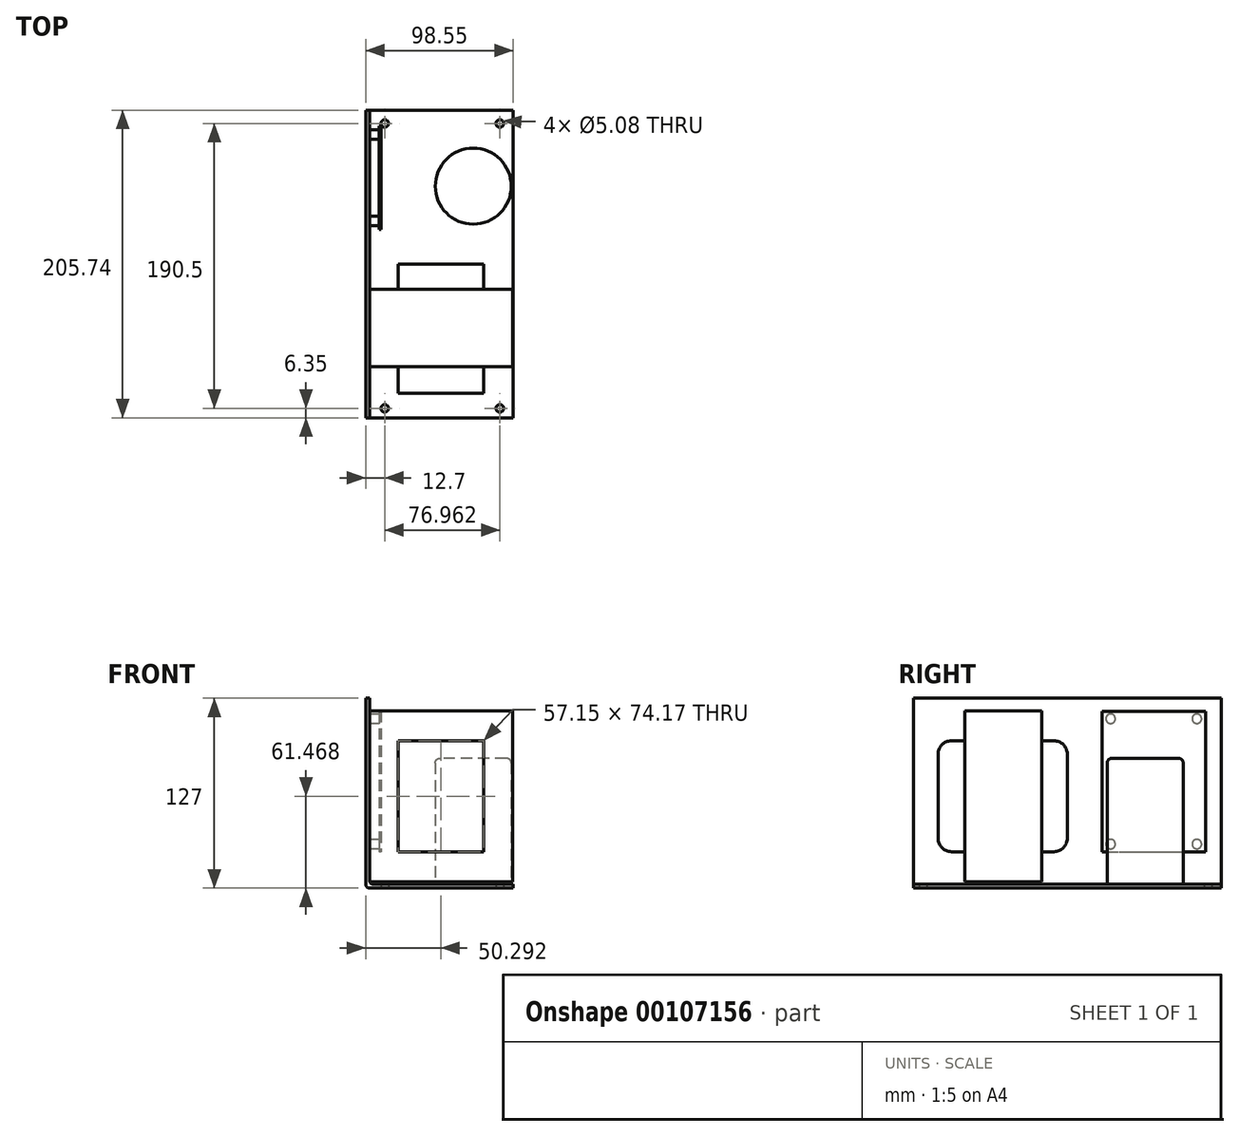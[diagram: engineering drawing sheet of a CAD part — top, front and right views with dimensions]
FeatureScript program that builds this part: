
annotation { "Feature Type Name" : "Feature", "Feature Type Description" : "" }
export const myFeature = defineFeature(function(context is Context, id is Id, definition is map)
    precondition{}
    {
        {
            var Q0;
            Q0=qCreatedBy(makeId("Front.planeOp"),FACE);
            var sketch = newSketch(context, id + "F0", { "sketchPlane" : qUnion([Q0])});
            skLineSegment(sketch, "E0.bottom", {"start": v(0, 0) * mm, "end": v(98.55, 0) * mm});
            skLineSegment(sketch, "E0.left", {"start": v(0, 0) * mm, "end": v(0, 127) * mm});
            skLineSegment(sketch, "E1.0", {"start": v(2.54, 2.54) * mm, "end": v(2.54, 127) * mm});
            skLineSegment(sketch, "E1.1", {"start": v(2.54, 2.54) * mm, "end": v(98.55, 2.54) * mm});
            skLineSegment(sketch, "E2", {"start": v(0, 127) * mm, "end": v(2.54, 127) * mm});
            skLineSegment(sketch, "E3", {"start": v(98.55, 2.54) * mm, "end": v(98.55, 0) * mm});
            skSolve(sketch);
        }
        {
            var Q0;
            Q0 = qSketchRegion(id + "F0", true);
            extrude(context, id + "F1", {"entities" : qUnion([Q0]), "depth" : 205.74 * mm});
        }
        {
            var Q0;
            Q0=makeQuery(id+"F1.opExtrude","SWEPT_FACE",FACE,{"disambiguationData":[OSD([sQuery(id+"F0.wireOp",EDGE,"E0.bottom")])]});
            var sketch = newSketch(context, id + "F2", { "sketchPlane" : qUnion([Q0])});
            skLineSegment(sketch, "E4.bottom", {"start": v(12.7, 199.4) * mm, "end": v(89.66, 199.4) * mm, "construction": true});
            skLineSegment(sketch, "E4.top", {"start": v(12.7, 8.89) * mm, "end": v(89.66, 8.89) * mm, "construction": true});
            skLineSegment(sketch, "E4.left", {"start": v(12.7, 199.4) * mm, "end": v(12.7, 8.89) * mm, "construction": true});
            skLineSegment(sketch, "E4.right", {"start": v(89.66, 199.4) * mm, "end": v(89.66, 8.89) * mm, "construction": true});
            skPoint(sketch, "E4.middle", {"position": v(51.18, 104.14) * mm});
            skSolve(sketch);
        }
        {
            var Q0;
            Q0=sQuery(id+"F2.wireOp",VERTEX,"E4.left.start");
            var Q1;
            Q1=sQuery(id+"F2.wireOp",VERTEX,"E4.right.start");
            var Q2;
            Q2=sQuery(id+"F2.wireOp",VERTEX,"E4.top.end");
            var Q3;
            Q3=sQuery(id+"F2.wireOp",VERTEX,"E4.left.end");
            var Q4;
            Q4=makeQuery(id+"F1.opExtrude","SWEPT_BODY",BODY,{"disambiguationData":[OSD([sQuery(id+"F0.wireOp",EDGE,"E0.bottom"),sQuery(id+"F0.wireOp",EDGE,"E0.left"),sQuery(id+"F0.wireOp",EDGE,"E1.0"),sQuery(id+"F0.wireOp",EDGE,"E1.1"),sQuery(id+"F0.wireOp",EDGE,"E2"),sQuery(id+"F0.wireOp",EDGE,"E3")])]});
            hole(context, id + "F3", {"style" : HoleStyle.SIMPLE, "endStyle" : HoleEndStyle.THROUGH, "holeDiameter" : 5.08 * mm, "locations" : qUnion([Q0, Q1, Q2, Q3]), "scope" : qUnion([Q4]), "isTappedThrough" : true});
        }
        {
            var Q0;
            Q0=makeQuery(id+"F1.opExtrude","SWEPT_EDGE",EDGE,{"disambiguationData":[OSD([sQuery(id+"F0.wireOp",EDGE,"E0.bottom"),sQuery(id+"F0.wireOp",EDGE,"E0.left")])]});
            var Q1;
            Q1=makeQuery(id+"F1.opExtrude","SWEPT_EDGE",EDGE,{"disambiguationData":[OSD([sQuery(id+"F0.wireOp",EDGE,"E1.0"),sQuery(id+"F0.wireOp",EDGE,"E1.1")])]});
            fillet(context, id + "F4", {"entities" : qUnion([Q0, Q1]), "radius" : 2.54 * mm, "tangentPropagation" : true, "allowEdgeOverflow" : false});
        }
        {
            var Q0;
            Q0=makeQuery(id+"F1.opExtrude","SWEPT_FACE",FACE,{"disambiguationData":[OSD([sQuery(id+"F0.wireOp",EDGE,"E1.0")])]});
            var sketch = newSketch(context, id + "F5", { "sketchPlane" : qUnion([Q0])});
            skLineSegment(sketch, "E5.bottom", {"start": v(-171.45, 118.62) * mm, "end": v(-119.89, 118.62) * mm});
            skLineSegment(sketch, "E5.top", {"start": v(-171.45, 4.32) * mm, "end": v(-119.89, 4.32) * mm});
            skLineSegment(sketch, "E5.left", {"start": v(-171.45, 118.62) * mm, "end": v(-171.45, 4.32) * mm});
            skLineSegment(sketch, "E5.right", {"start": v(-119.89, 118.62) * mm, "end": v(-119.89, 4.32) * mm});
            skSolve(sketch);
        }
        {
            var Q0;
            Q0 = qSketchRegion(id + "F5", true);
            extrude(context, id + "F6", {"entities" : qUnion([Q0]), "operationType" : NewBodyOperationType.ADD, "depth" : 95.5 * mm});
        }
        {
            var Q0;
            Q0=makeQuery(id+"F6.opExtrude","SWEPT_FACE",FACE,{"disambiguationData":[OSD([sQuery(id+"F5.wireOp",EDGE,"E5.left")])]});
            var sketch = newSketch(context, id + "F7", { "sketchPlane" : qUnion([Q0])});
            skLineSegment(sketch, "E6.bottom", {"start": v(21.72, 98.55) * mm, "end": v(78.87, 98.55) * mm});
            skLineSegment(sketch, "E6.top", {"start": v(21.72, 24.38) * mm, "end": v(78.87, 24.38) * mm});
            skLineSegment(sketch, "E6.left", {"start": v(21.72, 98.55) * mm, "end": v(21.72, 24.38) * mm});
            skLineSegment(sketch, "E6.right", {"start": v(78.87, 98.55) * mm, "end": v(78.87, 24.38) * mm});
            skPoint(sketch, "E6.middle", {"position": v(50.3, 61.47) * mm});
            skPoint(sketch, "E6.middle.positionSnap0", {"position": v(98.04, 61.47) * mm});
            skPoint(sketch, "E6.middle.positionSnap1", {"position": v(50.3, 118.62) * mm});
            skPoint(sketch, "E6.centerSnap0", {"position": v(98.04, 61.47) * mm});
            skPoint(sketch, "E6.centerSnap1", {"position": v(50.3, 118.62) * mm});
            skSolve(sketch);
        }
        {
            var Q0;
            Q0 = qSketchRegion(id + "F7", true);
            extrude(context, id + "F8", {"entities" : qUnion([Q0]), "operationType" : NewBodyOperationType.ADD, "depth" : 17.78 * mm, "hasSecondDirection" : true, "secondDirectionOppositeDirection" : true, "secondDirectionDepth" : 68.58 * mm});
        }
        {
            var Q0;
            Q0=makeQuery(id+"F1.opExtrude","SWEPT_FACE",FACE,{"disambiguationData":[OSD([sQuery(id+"F0.wireOp",EDGE,"E1.1")])]});
            var sketch = newSketch(context, id + "F9", { "sketchPlane" : qUnion([Q0])});
            skCircle(sketch, "E7", {"center": v(71.88, -50.8) * mm, "radius": 25.4 * mm});
            skSolve(sketch);
        }
        {
            var Q0;
            Q0 = qSketchRegion(id + "F9", true);
            extrude(context, id + "F10", {"entities" : qUnion([Q0]), "operationType" : NewBodyOperationType.ADD, "depth" : 84.33 * mm});
        }
        {
            var Q0;
            Q0=makeQuery(id+"F10.opExtrude","CAP_EDGE",EDGE,{"disambiguationData":[OSD([sQuery(id+"F9.wireOp",EDGE,"E7")])],"isStart":false});
            fillet(context, id + "F11", {"entities" : qUnion([Q0]), "radius" : 3.17 * mm, "tangentPropagation" : true, "allowEdgeOverflow" : false});
        }
        {
            var Q0;
            Q0=makeQuery(id+"F8.opExtrude","CAP_EDGE",EDGE,{"disambiguationData":[OSD([sQuery(id+"F7.wireOp",EDGE,"E6.bottom")])],"isStart":false});
            var Q1;
            Q1=makeQuery(id+"F8.opExtrude","CAP_EDGE",EDGE,{"disambiguationData":[OSD([sQuery(id+"F7.wireOp",EDGE,"E6.top")])],"isStart":false});
            var Q2;
            Q2=makeQuery(id+"F8.opExtrude","CAP_EDGE",EDGE,{"disambiguationData":[OSD([sQuery(id+"F7.wireOp",EDGE,"E6.bottom")])],"isStart":true});
            var Q3;
            Q3=makeQuery(id+"F8.opExtrude","CAP_EDGE",EDGE,{"disambiguationData":[OSD([sQuery(id+"F7.wireOp",EDGE,"E6.top")])],"isStart":true});
            fillet(context, id + "F12", {"entities" : qUnion([Q0, Q1, Q2, Q3]), "radius" : 8.9 * mm, "tangentPropagation" : true, "allowEdgeOverflow" : false});
        }
        {
            var Q0;
            Q0=makeQuery(id+"F1.opExtrude","SWEPT_FACE",FACE,{"disambiguationData":[OSD([sQuery(id+"F0.wireOp",EDGE,"E1.0")])]});
            var sketch = newSketch(context, id + "F13", { "sketchPlane" : qUnion([Q0])});
            skLineSegment(sketch, "E8.bottom", {"start": v(-73.91, 113.28) * mm, "end": v(-16.26, 113.28) * mm, "construction": true});
            skLineSegment(sketch, "E8.top", {"start": v(-73.91, 29.46) * mm, "end": v(-16.26, 29.46) * mm, "construction": true});
            skLineSegment(sketch, "E8.left", {"start": v(-73.91, 113.28) * mm, "end": v(-73.91, 29.46) * mm, "construction": true});
            skLineSegment(sketch, "E8.right", {"start": v(-16.26, 113.28) * mm, "end": v(-16.26, 29.46) * mm, "construction": true});
            skCircle(sketch, "E9", {"center": v(-73.91, 113.28) * mm, "radius": 3.18 * mm});
            skCircle(sketch, "E10", {"center": v(-16.26, 113.28) * mm, "radius": 3.18 * mm});
            skCircle(sketch, "E11", {"center": v(-16.26, 29.46) * mm, "radius": 3.18 * mm});
            skCircle(sketch, "E12", {"center": v(-73.91, 29.46) * mm, "radius": 3.18 * mm});
            skLineSegment(sketch, "E13", {"start": v(-45.09, 113.28) * mm, "end": v(-45.09, 71.37) * mm, "construction": true});
            skPoint(sketch, "E13.endSnap0", {"position": v(-73.91, 71.37) * mm});
            skLineSegment(sketch, "E14", {"start": v(-45.09, 71.37) * mm, "end": v(-73.91, 71.37) * mm, "construction": true});
            skLineSegment(sketch, "E15", {"start": v(-45.09, 29.46) * mm, "end": v(-45.09, 71.37) * mm, "construction": true});
            skLineSegment(sketch, "E16", {"start": v(-45.09, 71.37) * mm, "end": v(-16.26, 71.37) * mm, "construction": true});
            skSolve(sketch);
        }
        {
            var Q0;
            Q0 = qSketchRegion(id + "F13", true);
            extrude(context, id + "F14", {"entities" : qUnion([Q0]), "operationType" : NewBodyOperationType.ADD, "depth" : 6.35 * mm});
        }
        {
            var Q0;
            Q0=makeQuery(id+"F14.opExtrude","CAP_FACE",FACE,{"disambiguationData":[OSD([sQuery(id+"F13.wireOp",EDGE,"E10")])],"isStart":false});
            var sketch = newSketch(context, id + "F15", { "sketchPlane" : qUnion([Q0])});
            skLineSegment(sketch, "E17.bottom", {"start": v(-79.76, 118.36) * mm, "end": v(-10.41, 118.36) * mm});
            skLineSegment(sketch, "E17.top", {"start": v(-79.76, 24.38) * mm, "end": v(-10.41, 24.38) * mm});
            skLineSegment(sketch, "E17.left", {"start": v(-79.76, 118.36) * mm, "end": v(-79.76, 24.38) * mm});
            skLineSegment(sketch, "E17.right", {"start": v(-10.41, 118.36) * mm, "end": v(-10.41, 24.38) * mm});
            skPoint(sketch, "E17.middle", {"position": v(-45.09, 71.37) * mm});
            skSolve(sketch);
        }
        {
            var Q0;
            Q0 = qSketchRegion(id + "F15", true);
            extrude(context, id + "F16", {"entities" : qUnion([Q0]), "operationType" : NewBodyOperationType.ADD, "depth" : 1.52 * mm});
        }
    });
